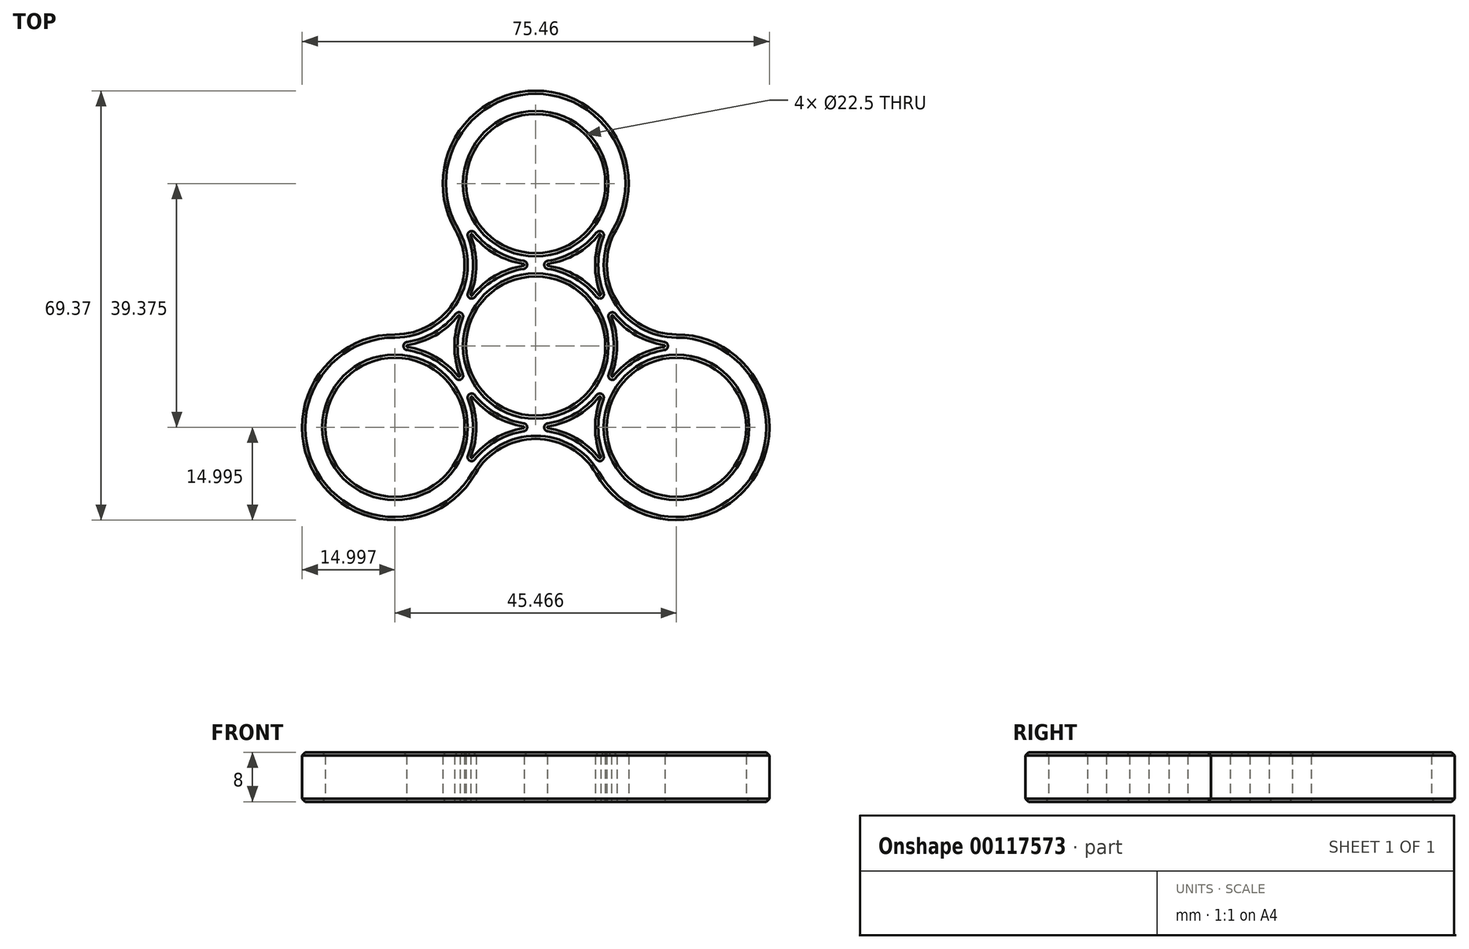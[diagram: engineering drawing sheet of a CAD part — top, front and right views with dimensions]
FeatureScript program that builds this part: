
annotation { "Feature Type Name" : "Feature", "Feature Type Description" : "" }
export const myFeature = defineFeature(function(context is Context, id is Id, definition is map)
    precondition{}
    {
        {
            var Q0;
            Q0=qCreatedBy(makeId("Top.planeOp"),FACE);
            var sketch = newSketch(context, id + "F0", { "sketchPlane" : qUnion([Q0])});
            skArc(sketch, "E0", {"start": v(9.74, 5.62) * mm, "mid": v(5.62, 9.74) * mm, "end": v(0, 11.25) * mm});
            skArc(sketch, "E1", {"start": v(0, 15) * mm, "mid": v(11.25, 26.25) * mm, "end": v(0, 37.5) * mm});
            skLineSegment(sketch, "E2", {"start": v(0, 41.25) * mm, "end": v(0, 37.5) * mm});
            skLineSegment(sketch, "E3", {"start": v(9.74, 5.62) * mm, "end": v(13, 7.5) * mm});
            skArc(sketch, "E4", {"start": v(13, 18.75) * mm, "mid": v(13, 33.75) * mm, "end": v(0, 41.25) * mm});
            skArc(sketch, "E5", {"start": v(13, 7.5) * mm, "mid": v(7.5, 13) * mm, "end": v(0, 15) * mm, "construction": true});
            skArc(sketch, "E6", {"start": v(13, 18.75) * mm, "mid": v(11.48, 13.12) * mm, "end": v(13, 7.5) * mm});
            skLineSegment(sketch, "E7.trimOffspring", {"start": v(0, 15) * mm, "end": v(0, 11.25) * mm});
            skLineSegment(sketch, "E8", {"start": v(0, 11.25) * mm, "end": v(9.74, 5.62) * mm, "construction": true});
            skLineSegment(sketch, "E9", {"start": v(0, 0) * mm, "end": v(9.74, 5.62) * mm, "construction": true});
            skLineSegment(sketch, "E10", {"start": v(0, 0) * mm, "end": v(0, 11.25) * mm, "construction": true});
            skSolve(sketch);
        }
        {
            var Q0;
            Q0 = qSketchRegion(id + "F0", true);
            extrude(context, id + "F1", {"entities" : qUnion([Q0]), "depth" : 8 * mm, "offsetDistance" : 25 * mm});
        }
        {
            var Q0;
            Q0=qCreatedBy(makeId("Top.planeOp"),FACE);
            var sketch = newSketch(context, id + "F2", { "sketchPlane" : qUnion([Q0])});
            skArc(sketch, "E11", {"start": v(2, 13.28) * mm, "mid": v(6.56, 14.88) * mm, "end": v(10.23, 18.03) * mm});
            skArc(sketch, "E12", {"start": v(10.5, 17.87) * mm, "mid": v(9.6, 13.12) * mm, "end": v(10.5, 8.38) * mm});
            skArc(sketch, "E13", {"start": v(10.23, 8.22) * mm, "mid": v(6.56, 11.37) * mm, "end": v(2, 12.97) * mm});
            skLineSegment(sketch, "E14", {"start": v(5.62, 9.74) * mm, "end": v(6.56, 11.37) * mm, "construction": true});
            skArc(sketch, "E15.filletArc", {"start": v(2, 13.28) * mm, "mid": v(1.87, 13.12) * mm, "end": v(2, 12.97) * mm});
            skArc(sketch, "E16.filletArc", {"start": v(10.5, 17.87) * mm, "mid": v(10.43, 18.06) * mm, "end": v(10.23, 18.03) * mm});
            skArc(sketch, "E17.filletArc", {"start": v(10.23, 8.22) * mm, "mid": v(10.43, 8.19) * mm, "end": v(10.5, 8.38) * mm});
            skLineSegment(sketch, "E18", {"start": v(10.43, 8.19) * mm, "end": v(11.37, 6.56) * mm, "construction": true});
            skSolve(sketch);
        }
        {
            var Q0;
            Q0 = qSketchRegion(id + "F2", true);
            extrude(context, id + "F3", {"entities" : qUnion([Q0]), "operationType" : NewBodyOperationType.REMOVE, "endBound" : BoundingType.THROUGH_ALL, "depth" : 25 * mm, "offsetDistance" : 25 * mm});
        }
        {
            var Q0;
            Q0=makeQuery(id+"F1.opExtrude","CAP_EDGE",EDGE,{"disambiguationData":[OSD([sQuery(id+"F0.wireOp",EDGE,"E6")])],"isStart":false});
            var Q1;
            Q1=makeQuery(id+"F1.opExtrude","CAP_EDGE",EDGE,{"disambiguationData":[OSD([sQuery(id+"F0.wireOp",EDGE,"E0")])],"isStart":false});
            var Q2;
            Q2=makeQuery(id+"F1.opExtrude","CAP_EDGE",EDGE,{"disambiguationData":[OSD([sQuery(id+"F0.wireOp",EDGE,"E0")])],"isStart":true});
            var Q3;
            Q3=makeQuery(id+"F1.opExtrude","CAP_EDGE",EDGE,{"disambiguationData":[OSD([sQuery(id+"F0.wireOp",EDGE,"E4")])],"isStart":true});
            var Q4;
            Q4=makeQuery(id+"F1.opExtrude","CAP_EDGE",EDGE,{"disambiguationData":[OSD([sQuery(id+"F0.wireOp",EDGE,"E1")])],"isStart":false});
            var Q5;
            Q5=makeQuery(id+"F1.opExtrude","CAP_EDGE",EDGE,{"disambiguationData":[OSD([sQuery(id+"F0.wireOp",EDGE,"E1")])],"isStart":true});
            var Q6;
            Q6=makeQuery(id+"F1.opExtrude","CAP_EDGE",EDGE,{"disambiguationData":[OSD([sQuery(id+"F0.wireOp",EDGE,"E4")])],"isStart":false});
            var Q7;
            Q7=makeQuery(id+"F1.opExtrude","CAP_EDGE",EDGE,{"disambiguationData":[OSD([sQuery(id+"F0.wireOp",EDGE,"E6")])],"isStart":true});
            var Q8;
            Q8=makeQuery(id+"F3.boolean.opBoolean","INTERSECT",EDGE,{"derivedFrom":[makeQuery(id+"F1.opExtrude","CAP_FACE",FACE,{"disambiguationData":[OSD([sQuery(id+"F0.wireOp",EDGE,"E0"),sQuery(id+"F0.wireOp",EDGE,"E1"),sQuery(id+"F0.wireOp",EDGE,"E2"),sQuery(id+"F0.wireOp",EDGE,"E3"),sQuery(id+"F0.wireOp",EDGE,"E4"),sQuery(id+"F0.wireOp",EDGE,"E6"),sQuery(id+"F0.wireOp",EDGE,"E7.trimOffspring")])],"isStart":false}),makeQuery(id+"F3.opExtrude","SWEPT_FACE",FACE,{"disambiguationData":[OSD([sQuery(id+"F2.wireOp",EDGE,"E12")])]})]});
            var Q9;
            Q9=makeQuery(id+"F3.boolean.opBoolean","COPY",EDGE,{"derivedFrom":makeQuery(id+"F3.opExtrude","CAP_EDGE",EDGE,{"disambiguationData":[OSD([sQuery(id+"F2.wireOp",EDGE,"E13")])],"isStart":true})});
            chamfer(context, id + "F4", {"entities" : qUnion([Q0, Q1, Q2, Q3, Q4, Q5, Q6, Q7, Q8, Q9]), "width" : .5 * mm, "tangentPropagation" : true});
        }
        {
            var Q0;
            Q0=makeQuery(id+"F1.opExtrude","SWEPT_BODY",BODY,{"disambiguationData":[OSD([sQuery(id+"F0.wireOp",EDGE,"E0"),sQuery(id+"F0.wireOp",EDGE,"E1"),sQuery(id+"F0.wireOp",EDGE,"E2"),sQuery(id+"F0.wireOp",EDGE,"E3"),sQuery(id+"F0.wireOp",EDGE,"E4"),sQuery(id+"F0.wireOp",EDGE,"E6"),sQuery(id+"F0.wireOp",EDGE,"E7.trimOffspring")])]});
            var Q1;
            Q1=qCreatedBy(makeId("Right.planeOp"),FACE);
            mirror(context, id + "F5", {"operationType" : NewBodyOperationType.ADD, "entities" : qUnion([Q0]), "mirrorPlane" : qUnion([Q1])});
        }
        {
            var Q0;
            Q0=makeQuery(id+"F1.opExtrude","SWEPT_BODY",BODY,{"disambiguationData":[OSD([sQuery(id+"F0.wireOp",EDGE,"E0"),sQuery(id+"F0.wireOp",EDGE,"E1"),sQuery(id+"F0.wireOp",EDGE,"E2"),sQuery(id+"F0.wireOp",EDGE,"E3"),sQuery(id+"F0.wireOp",EDGE,"E4"),sQuery(id+"F0.wireOp",EDGE,"E6"),sQuery(id+"F0.wireOp",EDGE,"E7.trimOffspring")])]});
            var Q1;
            {var subQ0=makeQuery(id+"F1.opExtrude","SWEPT_FACE",FACE,{"disambiguationData":[OSD([sQuery(id+"F0.wireOp",EDGE,"E0")])]});Q1=makeQuery(id+"F5.boolean.opBoolean","MERGE",FACE,{"derivedFrom":[subQ0,makeQuery(id+"F5.opPattern","COPY",FACE,{"derivedFrom":subQ0,"instanceName":"1"})]});}
            circularPattern(context, id + "F6", {"operationType" : NewBodyOperationType.ADD, "entities" : qUnion([Q0]), "axis" : qUnion([Q1]), "angle" : 360 * degree, "instanceCount" : 3, "equalSpace" : true, "computeTransformsWithoutBuiltin" : true});
        }
    });
